# Revit family: 2060568+2028034 Sylvania Lighting Fixture ASCENT 100 II ARCH 2700 4K DALI EMG 160 with IP44 Clear Glass
name_source: partatom
category: Lighting Fixtures
revit_build: Autodesk Revit 2016 (Build: 20150220_1215(x64)
units: mm (PartAtom-declared; Revit-internal decimal feet)

## family parameters
Cut with Voids When Loaded = No
Host = Face
Light Source = Yes
OmniClass Number = 23.80.70.11.17
OmniClass Title = Specialized Lighting by Location or Use
Part Type = Normal
Room Calculation Point = No
Round Connector Dimension = Use Diameter
Shared = No

## types (2) — shared parameters
Aperture_SYL = 160 mm  [stored 0.524934 ft]
Assembly Code = D5020200
AssetType = Fixed
Color Filter = 16777215
CutoutDiameter_SYL = 176 mm
Description = Direct LED retro fit for original LED 100 Arch (160) single CFL lamp offering Matching lumen levels and improved light distribution of original LED 100 CFL lamp equivalents Typically half the power consumption compared to CFL Up to 112lm/W 160mm aperture Architectural reflector accepts range of glass accessories from existing LED 100 Arch 160 offering HE, HO and VHO versions equivalent of single 1 x 18W, 1 x 32W, 1 x 42W
 Additional VVHO versions which offer the performance circa 2 x 32W equivalent
Diameter_SYL = 189 mm  [stored 0.620079 ft]
DiffuserRadius_SYL = 73 mm  [stored 0.239501 ft]
Dimming Lamp Color Temperature Shift = <None>
DocumentationLiterature = http://www.sylvania-lighting.com
DurationUnit = hours
ElectricShockClassification = Class II
Emit Shape Visible in Rendering = No
Emit from Circle Diameter = 146 mm  [stored 0.479003 ft]
EmittionSurface_SYL = 7 mm  [stored 0.0229659 ft]
ExpectedLife = 50000
HeightAcc_SYL = 7 mm  [stored 0.0229659 ft]
Height_SYL = 94 mm  [stored 0.308399 ft]
IfcExportAs = IfcLightFixtureType
IfcExportType = IfcLightFixtureType
ImpactProtectionIndex = IK02
IngressProtection = IP44
Keynote = 16500
Lamp = LED
LampColourRenderingIndex = 80
LampColourTemperature = 4000 K
LampMacAdamStep = 3
LampNominalLuminous = 2767 lm
LampsType = LED
LightOutputRatio = 100
LuminousEfficacy = 120 lm/W
Manufacturer = Feilo Sylvania
ManufacturerName = Feilo Sylvania
Material = aluminium housing, arcylic diffuser
Material_1_SYL = Aluminum_Sylvania_Ascent_White
Material_2_SYL = Aluminium_Sylvania_Ascent_Silver
Material_3_SYL = Polycarbonate_Sylvania_Ascent_Clear
Material_4_SYL = <By Category>
ModelNumber = 2060568+2028034
NominalHeight = 94 mm  [stored 0.308399 ft]
PowerConsumption = 23 W
RadiusAcc_SYL = 105 mm  [stored 0.344488 ft]
Radius_SYL = 94.5 mm  [stored 0.310039 ft]
ReflectorRadius_SYL = 80 mm  [stored 0.262467 ft]
Tilt Angle = -90°
URL = http://www.sylvania-lighting.com
VisibilityAccessory_SYL = Yes
Voltage = 0 V
Weight = 1.92 kg
WidthBezelAcc_SYL = 25 mm  [stored 0.082021 ft]
zero-valued in all types: Default Elevation, NominalLength, NominalWidth, PowerFactor

## per-type parameters (varying)
| type | Apparent Load | Model | ModelReference | Name | Photometric Web File | TypeName |
| 2060568+2028034 ASCT100 II ARCH 2700 4K DALI EMG 160 with IP44 Clear Glass | 23 VA | ASCENT 100 II ARCH 2700 4K DALI EMG 160 | ASCENT 100 II ARCH 2700 4K DALI EMG 160 | ASCENT 100 II ARCH 2700 4K DALI EMG 160 | 2060568.ies | ASCENT 100 II ARCH 2700 4K DALI EMG 160 |
| 2060568+2028034 ASCT100 II ARCH 2700 4K DALI EMG 160 with IP44 Clear Glass Emergency mode | 2 VA | ASCT100 II ARCH 2700 4K DALI EMG 160 with IP44 Clear Glass Emergency mode | ASCT100 II ARCH 2700 4K DALI EMG 160 with IP44 Clear Glass Emergency mode | ASCT100 II ARCH 2700 4K DALI EMG 160 with IP44 Clear Glass Emergency mode | 2060568EM.ies | ASCT100 II ARCH 2700 4K DALI EMG 160 with IP44 Clear Glass Emergency mode |

note: [stored X ft] marks values corroborated as IEEE doubles in the binary element streams (Revit-internal decimal feet)

## geometry (parser evidence)
native form markers: Sweep x2
no freeform markers — native parametric forms only
